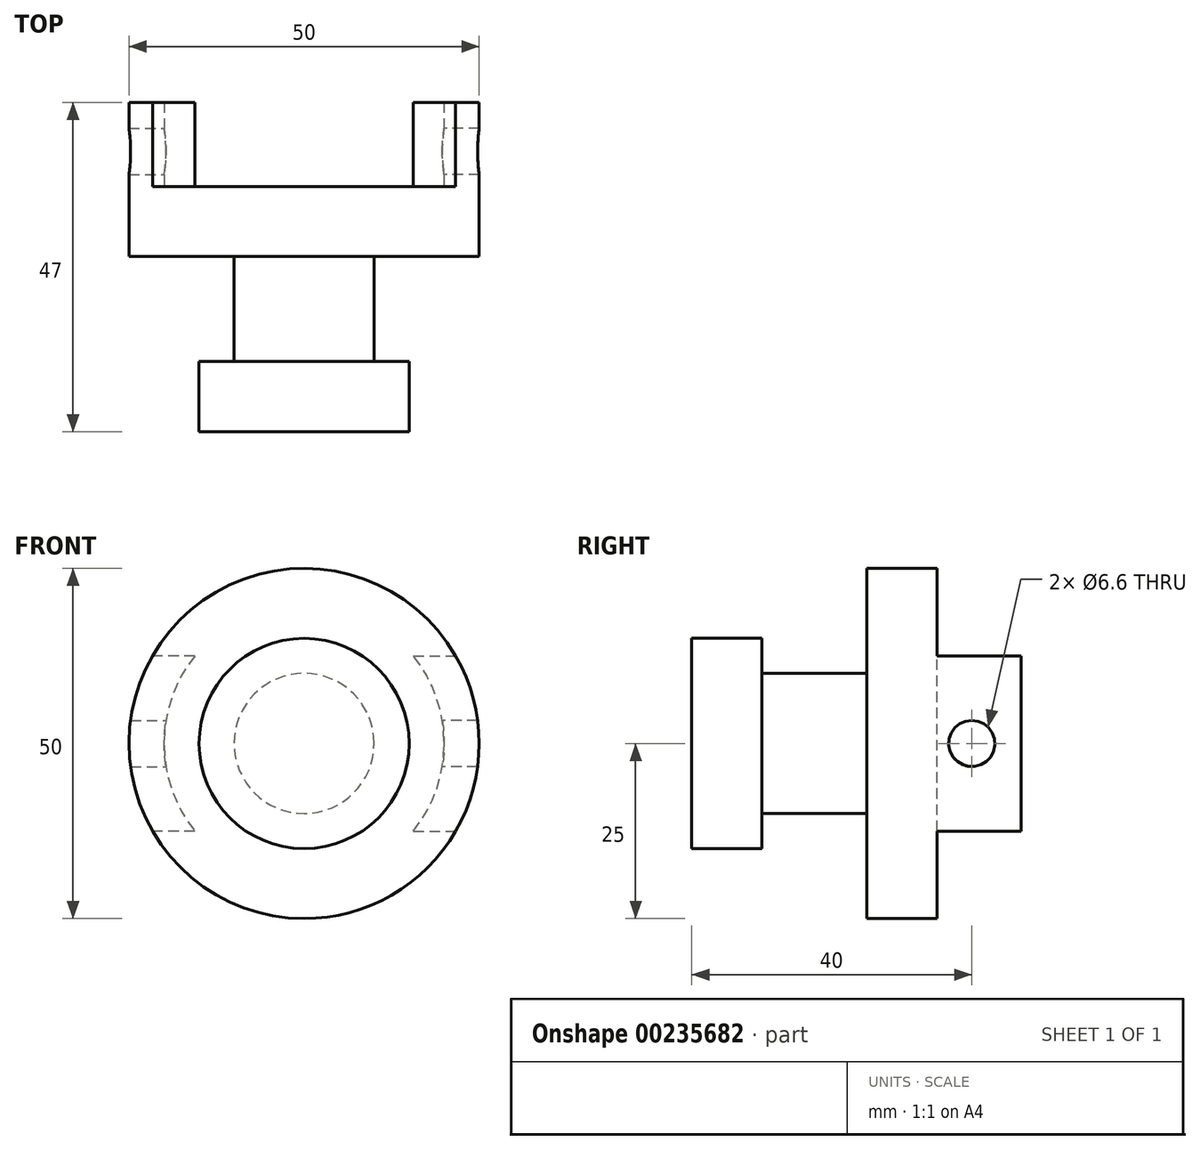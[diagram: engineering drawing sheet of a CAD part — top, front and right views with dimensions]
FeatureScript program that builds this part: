
annotation { "Feature Type Name" : "Feature", "Feature Type Description" : "" }
export const myFeature = defineFeature(function(context is Context, id is Id, definition is map)
    precondition{}
    {
        {
            var Q0;
            Q0=qCreatedBy(makeId("Front.planeOp"),FACE);
            var sketch = newSketch(context, id + "F0", { "sketchPlane" : qUnion([Q0])});
            skCircle(sketch, "E0", {"center": v(0, 0) * mm, "radius": 25 * mm});
            skSolve(sketch);
        }
        {
            var Q0;
            Q0 = qSketchRegion(id + "F0", true);
            extrude(context, id + "F1", {"entities" : qUnion([Q0]), "depth" : 10 * mm, "offsetDistance" : 25 * mm});
        }
        {
            var Q0;
            Q0=qCreatedBy(makeId("Front.planeOp"),FACE);
            var sketch = newSketch(context, id + "F2", { "sketchPlane" : qUnion([Q0])});
            skArc(sketch, "E1.0", {"start": v(15.61, -12.5) * mm, "mid": v(20, 0) * mm, "end": v(15.61, 12.5) * mm});
            skArc(sketch, "E1.1", {"start": v(21.65, -12.5) * mm, "mid": v(25, 0) * mm, "end": v(21.65, 12.5) * mm});
            skLineSegment(sketch, "E2", {"start": v(15.61, -12.5) * mm, "end": v(21.65, -12.5) * mm});
            skLineSegment(sketch, "E3", {"start": v(15.61, 12.5) * mm, "end": v(21.65, 12.5) * mm});
            skSolve(sketch);
        }
        {
            var Q0;
            Q0 = qSketchRegion(id + "F2", true);
            extrude(context, id + "F3", {"entities" : qUnion([Q0]), "operationType" : NewBodyOperationType.ADD, "oppositeDirection" : true, "depth" : 12 * mm, "offsetDistance" : 25 * mm});
        }
        {
            var Q0;
            Q0=makeQuery(id+"F1.opExtrude","SWEPT_BODY",BODY,{"disambiguationData":[OSD([sQuery(id+"F0.wireOp",EDGE,"E0"),sQuery(id+"F0.wireOp",EDGE,"84T1Tn9L-JVOl-qyF8-Ftna-1iBVImejSwln")])]});
            var Q1;
            Q1=qCreatedBy(makeId("Right.planeOp"),FACE);
            mirror(context, id + "F4", {"operationType" : NewBodyOperationType.ADD, "entities" : qUnion([Q0]), "mirrorPlane" : qUnion([Q1])});
        }
        {
            var Q0;
            Q0=qCreatedBy(makeId("Right.planeOp"),FACE);
            var sketch = newSketch(context, id + "F5", { "sketchPlane" : qUnion([Q0])});
            skCircle(sketch, "E4", {"center": v(5, 0) * mm, "radius": 3 * mm});
            skSolve(sketch);
        }
        {
            var Q0;
            Q0=sQuery(id+"F5.wireOp",VERTEX,"E4.center");
            var Q1;
            Q1=makeQuery(id+"F1.opExtrude","SWEPT_BODY",BODY,{"disambiguationData":[OSD([sQuery(id+"F0.wireOp",EDGE,"E0"),sQuery(id+"F0.wireOp",EDGE,"84T1Tn9L-JVOl-qyF8-Ftna-1iBVImejSwln")])]});
            hole(context, id + "F6", {"style" : HoleStyle.SIMPLE, "endStyle" : HoleEndStyle.THROUGH, "oppositeDirection" : true, "standardTappedOrClearance" : lookupTablePath({ "standard" : "ISO", "fit" : "Normal", "size" : "M6", "type" : "Clearance" }), "standardBlindInLast" : lookupTablePath({ "fit" : "Standard", "standard" : "ISO", "size" : "M6", "type" : "Clearance" }), "holeDiameter" : 6.6 * mm, "locations" : qUnion([Q0]), "scope" : qUnion([Q1]), "isTappedThrough" : true});
        }
        {
            var Q0;
            Q0=qCreatedBy(makeId("Right.planeOp"),FACE);
            var sketch = newSketch(context, id + "F7", { "sketchPlane" : qUnion([Q0])});
            skCircle(sketch, "E5", {"center": v(5, 0) * mm, "radius": 3 * mm});
            skSolve(sketch);
        }
        {
            var Q0;
            Q0=sQuery(id+"F7.wireOp",VERTEX,"E5.center");
            var Q1;
            Q1=makeQuery(id+"F1.opExtrude","SWEPT_BODY",BODY,{"disambiguationData":[OSD([sQuery(id+"F0.wireOp",EDGE,"E0"),sQuery(id+"F0.wireOp",EDGE,"84T1Tn9L-JVOl-qyF8-Ftna-1iBVImejSwln")])]});
            hole(context, id + "F8", {"style" : HoleStyle.SIMPLE, "endStyle" : HoleEndStyle.THROUGH, "standardTappedOrClearance" : lookupTablePath({ "standard" : "ISO", "fit" : "Normal", "size" : "M6", "type" : "Clearance" }), "standardBlindInLast" : lookupTablePath({ "fit" : "Standard", "standard" : "ISO", "size" : "M6", "type" : "Clearance" }), "holeDiameter" : 6.6 * mm, "locations" : qUnion([Q0]), "scope" : qUnion([Q1]), "isTappedThrough" : true});
        }
        {
            var Q0;
            Q0=qCreatedBy(makeId("Right.planeOp"),FACE);
            var sketch = newSketch(context, id + "F9", { "sketchPlane" : qUnion([Q0])});
            skLineSegment(sketch, "E6", {"start": v(-10, 10) * mm, "end": v(-25, 10) * mm});
            skLineSegment(sketch, "E7", {"start": v(-25, 10) * mm, "end": v(-25, 15) * mm});
            skLineSegment(sketch, "E8", {"start": v(-10, 0) * mm, "end": v(-35, 0) * mm});
            skLineSegment(sketch, "E9", {"start": v(-35, 0) * mm, "end": v(-35, 15) * mm});
            skLineSegment(sketch, "E10", {"start": v(-35, 15) * mm, "end": v(-25, 15) * mm});
            skLineSegment(sketch, "E11", {"start": v(-10, 10) * mm, "end": v(-10, 0) * mm});
            skSolve(sketch);
        }
        {
            var Q0;
            Q0 = qSketchRegion(id + "F9", true);
            var Q1;
            Q1=sQuery(id+"F9.wireOp",EDGE,"E8");
            revolve(context, id + "F10", {"operationType" : NewBodyOperationType.ADD, "entities" : qUnion([Q0]), "axis" : qUnion([Q1]), "revolveType" : RevolveType.FULL});
        }
    });
